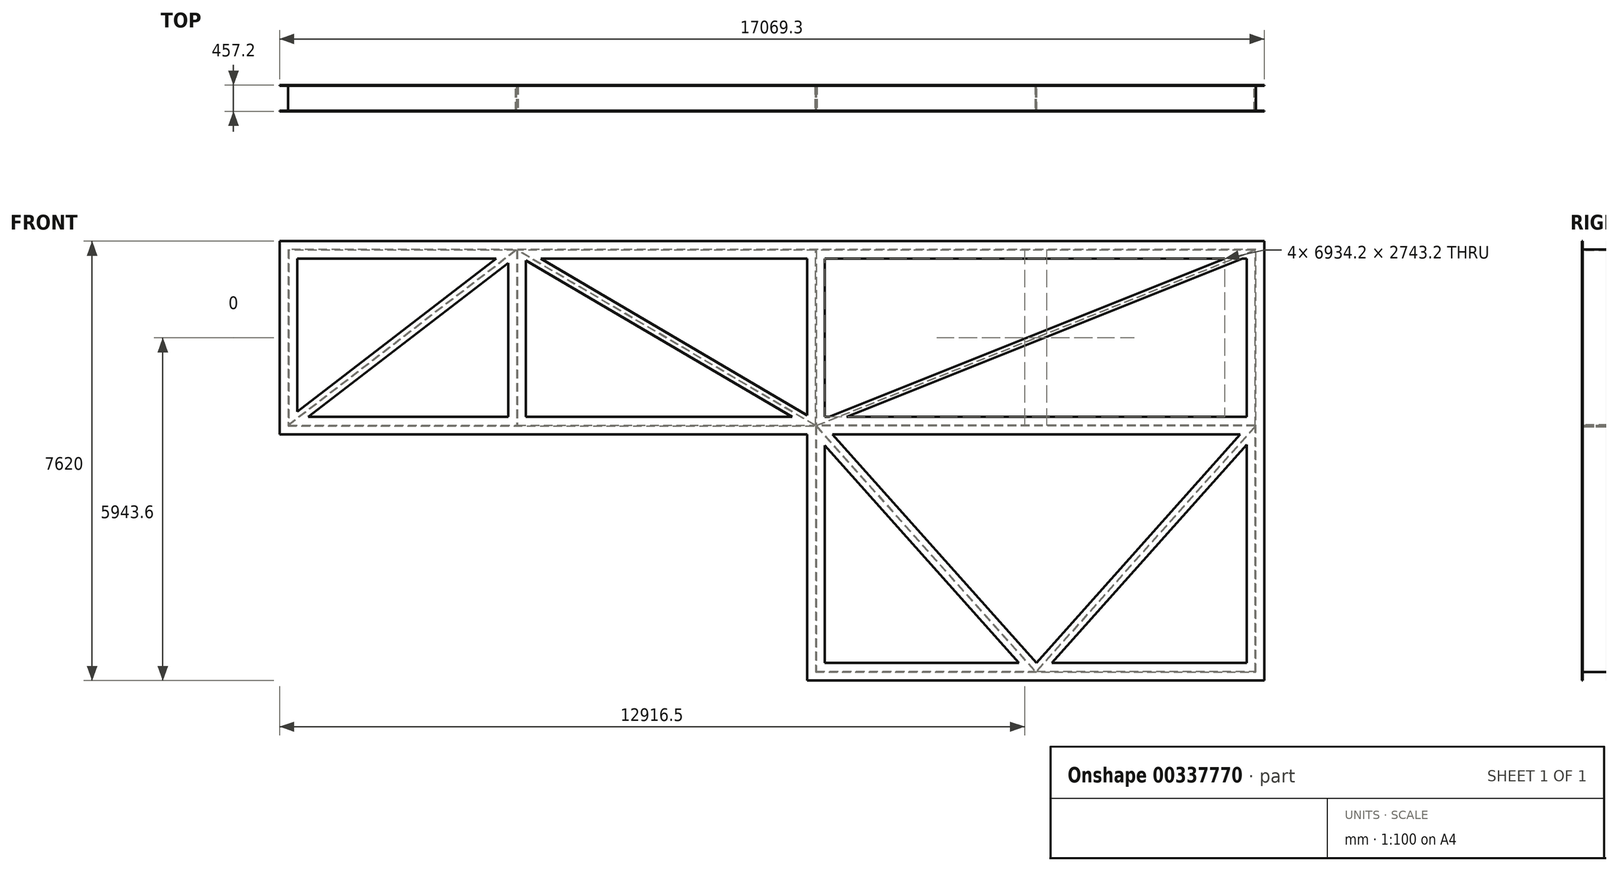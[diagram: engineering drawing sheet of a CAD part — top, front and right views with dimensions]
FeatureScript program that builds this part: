
annotation { "Feature Type Name" : "Feature", "Feature Type Description" : "" }
export const myFeature = defineFeature(function(context is Context, id is Id, definition is map)
    precondition{}
    {
        {
            var Q0;
            Q0=qCreatedBy(makeId("Front.planeOp"),FACE);
            var sketch = newSketch(context, id + "F0", { "sketchPlane" : qUnion([Q0])});
            skLineSegment(sketch, "E0.bottom", {"start": v(0, 0) * mm, "end": v(-9144, 0) * mm});
            skLineSegment(sketch, "E0.top", {"start": v(0, 3048) * mm, "end": v(-9144, 3048) * mm});
            skLineSegment(sketch, "E0.left", {"start": v(0, 0) * mm, "end": v(0, 3048) * mm});
            skLineSegment(sketch, "E0.right", {"start": v(-9144, 0) * mm, "end": v(-9144, 3048) * mm});
            skLineSegment(sketch, "E1", {"start": v(-5181.6, 0) * mm, "end": v(-5181.6, 3048) * mm});
            skLineSegment(sketch, "E2", {"start": v(-5181.6, 3048) * mm, "end": v(0, 0) * mm});
            skLineSegment(sketch, "E3", {"start": v(0, 3048) * mm, "end": v(7620, 3048) * mm});
            skLineSegment(sketch, "E4", {"start": v(7620, 3048) * mm, "end": v(7620, -4267.2) * mm});
            skLineSegment(sketch, "E5", {"start": v(7620, -4267.2) * mm, "end": v(0, -4267.2) * mm});
            skLineSegment(sketch, "E6", {"start": v(0, -4267.2) * mm, "end": v(0, 0) * mm});
            skLineSegment(sketch, "E7", {"start": v(0, 0) * mm, "end": v(3810, -4267.2) * mm});
            skLineSegment(sketch, "E8", {"start": v(3810, -4267.2) * mm, "end": v(7620, 0) * mm});
            skPoint(sketch, "E8.endSnap0", {"position": v(7620, -609.6) * mm});
            skLineSegment(sketch, "E9", {"start": v(7620, 0) * mm, "end": v(0, 0) * mm});
            skLineSegment(sketch, "E10", {"start": v(0, 0) * mm, "end": v(7620, 3048) * mm});
            skLineSegment(sketch, "E11", {"start": v(-5181.6, 3048) * mm, "end": v(-9144, 0) * mm});
            skSolve(sketch);
        }
        {
            var Q0;
            Q0=qCreatedBy(makeId("Front.planeOp"),FACE);
            var sketch = newSketch(context, id + "F1", { "sketchPlane" : qUnion([Q0])});
            skLineSegment(sketch, "E12.0", {"start": v(0, 3048) * mm, "end": v(-9144, 3048) * mm});
            skLineSegment(sketch, "E12.1", {"start": v(0, 3048) * mm, "end": v(7620, 3048) * mm});
            skLineSegment(sketch, "E12.2", {"start": v(7620, 3048) * mm, "end": v(7620, -4267.2) * mm});
            skLineSegment(sketch, "E12.3", {"start": v(7620, -4267.2) * mm, "end": v(0, -4267.2) * mm});
            skLineSegment(sketch, "E12.4", {"start": v(0, -4267.2) * mm, "end": v(0, 0) * mm});
            skLineSegment(sketch, "E12.5", {"start": v(0, 0) * mm, "end": v(-9144, 0) * mm});
            skLineSegment(sketch, "E13", {"start": v(-9144, 3048) * mm, "end": v(-9144, 0) * mm});
            skSolve(sketch);
        }
        {
            var Q0;
            Q0=qCreatedBy(makeId("Top.planeOp"),FACE);
            var sketch = newSketch(context, id + "F2", { "sketchPlane" : qUnion([Q0])});
            skLineSegment(sketch, "E14.bottom", {"start": v(6.35, 228.6) * mm, "end": v(-6.35, 228.6) * mm});
            skLineSegment(sketch, "E14.top", {"start": v(6.35, -228.6) * mm, "end": v(-6.35, -228.6) * mm});
            skLineSegment(sketch, "E14.left", {"start": v(6.35, 215.9) * mm, "end": v(6.35, -215.9) * mm});
            skLineSegment(sketch, "E14.right", {"start": v(-6.35, 215.9) * mm, "end": v(-6.35, -215.9) * mm});
            skPoint(sketch, "E14.middle", {"position": v(0, 0) * mm});
            skLineSegment(sketch, "E15", {"start": v(0, 286.38) * mm, "end": v(0, -378.6) * mm, "construction": true});
            skLineSegment(sketch, "E16.bottom", {"start": v(152.4, -228.6) * mm, "end": v(6.35, -228.6) * mm});
            skLineSegment(sketch, "E16.top", {"start": v(152.4, -215.9) * mm, "end": v(6.35, -215.9) * mm});
            skLineSegment(sketch, "E16.left", {"start": v(152.4, -228.6) * mm, "end": v(152.4, -215.9) * mm});
            skLineSegment(sketch, "E16.right", {"start": v(-152.4, -228.6) * mm, "end": v(-152.4, -215.9) * mm});
            skLineSegment(sketch, "E17.MirrorCS", {"start": v(-152.4, 228.6) * mm, "end": v(-152.4, 215.9) * mm});
            skLineSegment(sketch, "E18.MirrorCS", {"start": v(152.4, 228.6) * mm, "end": v(152.4, 215.9) * mm});
            skLineSegment(sketch, "E19.MirrorCS", {"start": v(6.35, 228.6) * mm, "end": v(0, 228.6) * mm});
            skLineSegment(sketch, "E20.MirrorCS", {"start": v(152.4, 228.6) * mm, "end": v(6.35, 228.6) * mm});
            skLineSegment(sketch, "E21.MirrorCS", {"start": v(152.4, 215.9) * mm, "end": v(6.35, 215.9) * mm});
            skLineSegment(sketch, "E22.trimOffspring", {"start": v(-6.35, -215.9) * mm, "end": v(-152.4, -215.9) * mm});
            skLineSegment(sketch, "E23.trimOffspring", {"start": v(-6.35, -228.6) * mm, "end": v(-152.4, -228.6) * mm});
            skLineSegment(sketch, "E24.trimOffspring", {"start": v(-6.35, 228.6) * mm, "end": v(-152.4, 228.6) * mm});
            skLineSegment(sketch, "E25.trimOffspring", {"start": v(-6.35, 215.9) * mm, "end": v(-152.4, 215.9) * mm});
            skSolve(sketch);
        }
        {
            var Q0;
            Q0 = qSketchRegion(id + "F2", true);
            var Q1;
            Q1=sQuery(id+"F1.wireOp",EDGE,"E12.4");
            var Q2;
            Q2=sQuery(id+"F1.wireOp",EDGE,"E12.3");
            var Q3;
            Q3=sQuery(id+"F1.wireOp",EDGE,"E12.2");
            var Q4;
            Q4=sQuery(id+"F1.wireOp",EDGE,"E12.1");
            var Q5;
            Q5=sQuery(id+"F1.wireOp",EDGE,"E12.0");
            var Q6;
            Q6=sQuery(id+"F1.wireOp",EDGE,"E13");
            var Q7;
            Q7=sQuery(id+"F1.wireOp",EDGE,"E12.5");
            sweep(context, id + "F3", {"profiles" : qUnion([Q0]), "path" : qUnion([Q1, Q2, Q3, Q4, Q5, Q6, Q7])});
        }
        {
            var Q0;
            Q0 = qSketchRegion(id + "F2", true);
            var Q1;
            Q1=sQuery(id+"F0.wireOp",EDGE,"E0.left");
            sweep(context, id + "F4", {"operationType" : NewBodyOperationType.ADD, "profiles" : qUnion([Q0]), "path" : qUnion([Q1])});
        }
        {
            var Q0;
            Q0 = qSketchRegion(id + "F2", true);
            var Q1;
            Q1=sQuery(id+"F0.wireOp",EDGE,"E10");
            sweep(context, id + "F5", {"operationType" : NewBodyOperationType.ADD, "profiles" : qUnion([Q0]), "path" : qUnion([Q1])});
        }
        {
            var Q0;
            Q0 = qSketchRegion(id + "F2", true);
            var Q1;
            Q1=sQuery(id+"F0.wireOp",EDGE,"E2");
            sweep(context, id + "F6", {"operationType" : NewBodyOperationType.ADD, "profiles" : qUnion([Q0]), "path" : qUnion([Q1])});
        }
        {
            var Q0;
            Q0 = qSketchRegion(id + "F2", true);
            var Q1;
            Q1=sQuery(id+"F0.wireOp",EDGE,"E7");
            sweep(context, id + "F7", {"operationType" : NewBodyOperationType.ADD, "profiles" : qUnion([Q0]), "path" : qUnion([Q1])});
        }
        {
            var Q0;
            Q0=makeQuery(id+"F3.opSweep","SWEPT_FACE",FACE,{"disambiguationData":[OSD([sQuery(id+"F1.wireOp",EDGE,"E12.0"),sQuery(id+"F2.wireOp",EDGE,"E14.right")])]});
            var sketch = newSketch(context, id + "F8", { "sketchPlane" : qUnion([Q0])});
            skLineSegment(sketch, "E26.bottom", {"start": v(-5175.8, 228.6) * mm, "end": v(-5188.5, 228.6) * mm});
            skLineSegment(sketch, "E26.top", {"start": v(-5175.8, -228.6) * mm, "end": v(-5188.5, -228.6) * mm});
            skLineSegment(sketch, "E26.left", {"start": v(-5175.8, 215.9) * mm, "end": v(-5175.8, -215.9) * mm});
            skLineSegment(sketch, "E26.right", {"start": v(-5188.5, 215.9) * mm, "end": v(-5188.5, -215.9) * mm});
            skPoint(sketch, "E26.middle", {"position": v(-5182.15, 0) * mm});
            skLineSegment(sketch, "E27", {"start": v(-5182.15, 290.7) * mm, "end": v(-5182.15, -374.3) * mm, "construction": true});
            skLineSegment(sketch, "E28.bottom", {"start": v(-5029.75, -228.6) * mm, "end": v(-5175.8, -228.6) * mm});
            skLineSegment(sketch, "E28.top", {"start": v(-5029.75, -215.9) * mm, "end": v(-5175.8, -215.9) * mm});
            skLineSegment(sketch, "E28.left", {"start": v(-5029.75, -228.6) * mm, "end": v(-5029.75, -215.9) * mm});
            skLineSegment(sketch, "E28.right", {"start": v(-5334.55, -228.6) * mm, "end": v(-5334.55, -215.9) * mm});
            skLineSegment(sketch, "E29.MirrorCS", {"start": v(-5334.55, 228.6) * mm, "end": v(-5334.55, 215.9) * mm});
            skLineSegment(sketch, "E30.MirrorCS", {"start": v(-5029.75, 228.6) * mm, "end": v(-5029.75, 215.9) * mm});
            skLineSegment(sketch, "E31.MirrorCS", {"start": v(-5029.75, 228.6) * mm, "end": v(-5175.8, 228.6) * mm});
            skLineSegment(sketch, "E32.MirrorCS", {"start": v(-5029.75, 215.9) * mm, "end": v(-5175.8, 215.9) * mm});
            skLineSegment(sketch, "E33.trimOffspring", {"start": v(-5188.5, -215.9) * mm, "end": v(-5334.55, -215.9) * mm});
            skLineSegment(sketch, "E34.trimOffspring", {"start": v(-5188.5, -228.6) * mm, "end": v(-5334.55, -228.6) * mm});
            skLineSegment(sketch, "E35.trimOffspring", {"start": v(-5188.5, 228.6) * mm, "end": v(-5334.55, 228.6) * mm});
            skLineSegment(sketch, "E36.trimOffspring", {"start": v(-5188.5, 215.9) * mm, "end": v(-5334.55, 215.9) * mm});
            skSolve(sketch);
        }
        {
            var Q0;
            Q0 = qSketchRegion(id + "F8", true);
            var Q1;
            Q1=sQuery(id+"F0.wireOp",EDGE,"E1");
            sweep(context, id + "F9", {"operationType" : NewBodyOperationType.ADD, "profiles" : qUnion([Q0]), "path" : qUnion([Q1])});
        }
        {
            var Q0;
            Q0 = qSketchRegion(id + "F8", true);
            var Q1;
            Q1=sQuery(id+"F0.wireOp",EDGE,"E11");
            sweep(context, id + "F10", {"operationType" : NewBodyOperationType.ADD, "profiles" : qUnion([Q0]), "path" : qUnion([Q1])});
        }
        {
            var Q0;
            Q0=makeQuery(id+"F3.opSweep","SWEPT_FACE",FACE,{"disambiguationData":[OSD([sQuery(id+"F1.wireOp",EDGE,"E12.2"),sQuery(id+"F2.wireOp",EDGE,"E14.right")])]});
            var sketch = newSketch(context, id + "F11", { "sketchPlane" : qUnion([Q0])});
            skLineSegment(sketch, "E37.bottom", {"start": v(228.6, -6.35) * mm, "end": v(228.6, 6.35) * mm});
            skLineSegment(sketch, "E37.top", {"start": v(-228.6, -6.35) * mm, "end": v(-228.6, 6.35) * mm});
            skLineSegment(sketch, "E37.left", {"start": v(215.9, -6.35) * mm, "end": v(-215.9, -6.35) * mm});
            skLineSegment(sketch, "E37.right", {"start": v(215.9, 6.35) * mm, "end": v(-215.9, 6.35) * mm});
            skPoint(sketch, "E37.middle", {"position": v(0, 0) * mm});
            skLineSegment(sketch, "E38", {"start": v(286.38, 0) * mm, "end": v(-378.6, 0) * mm, "construction": true});
            skLineSegment(sketch, "E39.bottom", {"start": v(-228.6, -152.4) * mm, "end": v(-228.6, -6.35) * mm});
            skLineSegment(sketch, "E39.top", {"start": v(-215.9, -152.4) * mm, "end": v(-215.9, -6.35) * mm});
            skLineSegment(sketch, "E39.left", {"start": v(-228.6, -152.4) * mm, "end": v(-215.9, -152.4) * mm});
            skLineSegment(sketch, "E39.right", {"start": v(-228.6, 152.4) * mm, "end": v(-215.9, 152.4) * mm});
            skLineSegment(sketch, "E40.MirrorCS", {"start": v(228.6, 152.4) * mm, "end": v(215.9, 152.4) * mm});
            skLineSegment(sketch, "E41.MirrorCS", {"start": v(228.6, -152.4) * mm, "end": v(215.9, -152.4) * mm});
            skLineSegment(sketch, "E42.MirrorCS", {"start": v(228.6, -6.35) * mm, "end": v(228.6, 0) * mm});
            skLineSegment(sketch, "E43.MirrorCS", {"start": v(228.6, -152.4) * mm, "end": v(228.6, -6.35) * mm});
            skLineSegment(sketch, "E44.MirrorCS", {"start": v(215.9, -152.4) * mm, "end": v(215.9, -6.35) * mm});
            skLineSegment(sketch, "E45.trimOffspring", {"start": v(-215.9, 6.35) * mm, "end": v(-215.9, 152.4) * mm});
            skLineSegment(sketch, "E46.trimOffspring", {"start": v(-228.6, 6.35) * mm, "end": v(-228.6, 152.4) * mm});
            skLineSegment(sketch, "E47.trimOffspring", {"start": v(228.6, 6.35) * mm, "end": v(228.6, 152.4) * mm});
            skLineSegment(sketch, "E48.trimOffspring", {"start": v(215.9, 6.35) * mm, "end": v(215.9, 152.4) * mm});
            skSolve(sketch);
        }
        {
            var Q0;
            Q0 = qSketchRegion(id + "F11", true);
            var Q1;
            Q1=sQuery(id+"F0.wireOp",EDGE,"E9");
            sweep(context, id + "F12", {"operationType" : NewBodyOperationType.ADD, "profiles" : qUnion([Q0]), "path" : qUnion([Q1])});
        }
        {
            var Q0;
            Q0 = qSketchRegion(id + "F11", true);
            var Q1;
            Q1=sQuery(id+"F0.wireOp",EDGE,"E8");
            sweep(context, id + "F13", {"operationType" : NewBodyOperationType.ADD, "profiles" : qUnion([Q0]), "path" : qUnion([Q1])});
        }
    });
